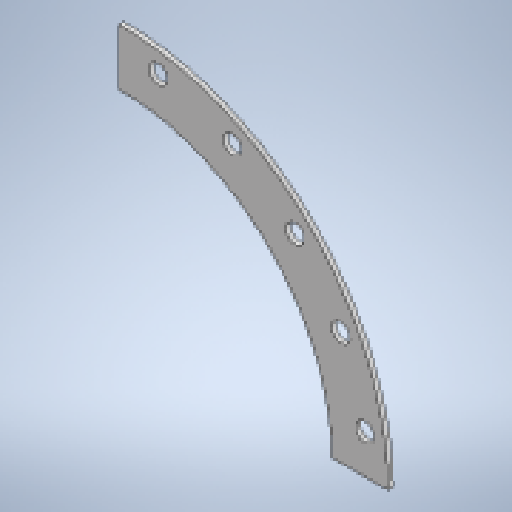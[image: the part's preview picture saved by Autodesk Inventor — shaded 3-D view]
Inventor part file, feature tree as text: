
AUTODESK INVENTOR PART (.ipt)
format: ipt  version: 2025.1 (Build 291241020, 241B)  size: 205,312 bytes
history: native  units: mm
features: sketch x2, other x2, extrude x1, pattern_circular x1, projected_geometry x1
ambient origin geometry x8: Origin, YZ Plane, XZ Plane, XY Plane, X Axis, Y Axis, Z Axis, Center Point
bodies: Solid1 (feature_tree)
feature tree (7):
  extrude  "Extrusion1"  Depth=6.0mm TaperAngle=0.0deg
  pattern_circular  "Circular Pattern1"  Count=53  [1 undecoded]
  sketch  "Sketch1"  dims[d0=512.0mm d1=670.0mm d2=6.0mm d3=0.0mm d4=530.0mm]
  sketch  "Sketch2"  dims[d5=310.0mm d6=1.570796mm d7=23.0mm d8=8.0mm d9=8.0mm d10=0.0mm d11=200.0mm d12=360.0deg]
  projected_geometry  "Projected Loop1"
  other  "Cut1"
  other  "Definition1"
note: 1 required parameter value undecoded (feature->parameter linkage not recoverable at this tier; creation-order binding heuristic only, values carry confidence <= 0.55)
